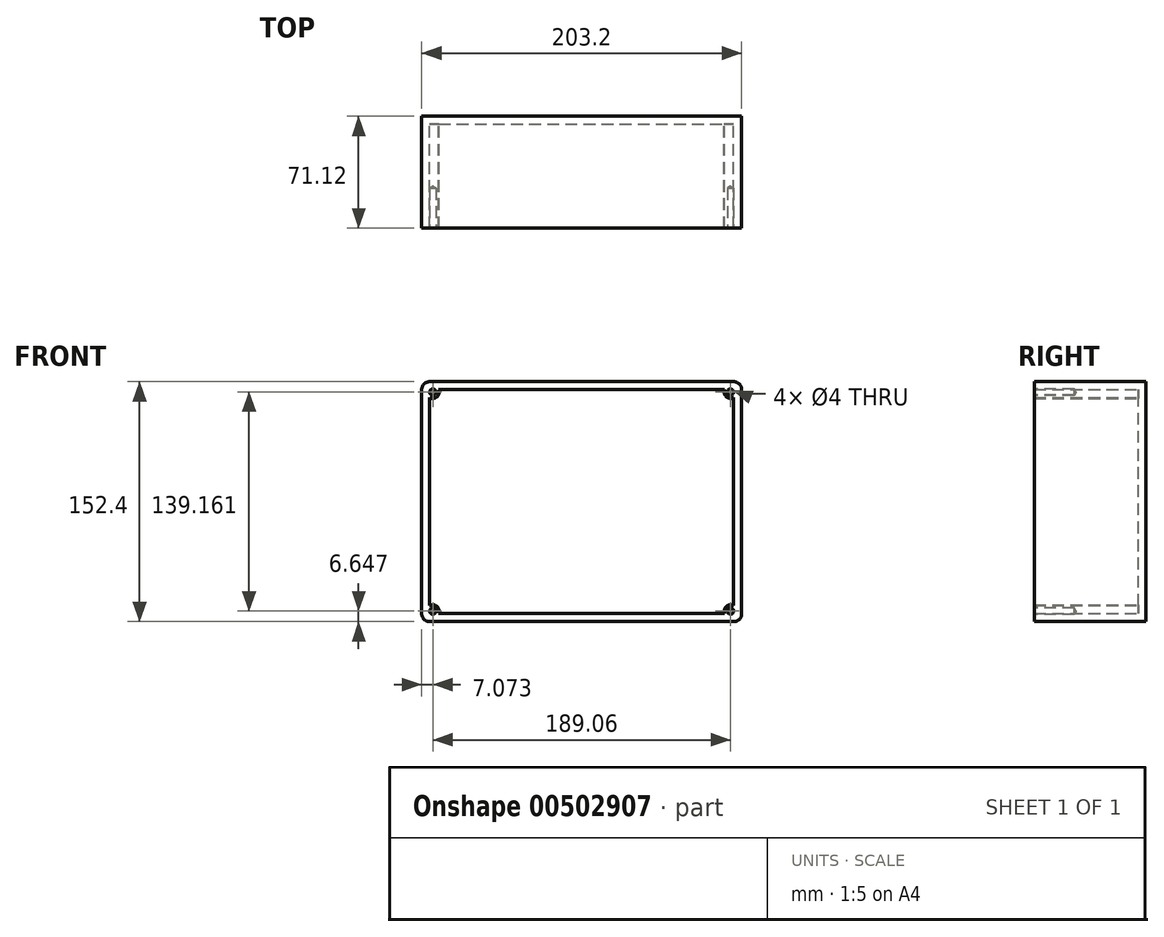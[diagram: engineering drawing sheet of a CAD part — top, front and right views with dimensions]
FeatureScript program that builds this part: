
annotation { "Feature Type Name" : "Feature", "Feature Type Description" : "" }
export const myFeature = defineFeature(function(context is Context, id is Id, definition is map)
    precondition{}
    {
        {
            var Q0;
            Q0=qCreatedBy(makeId("Front.planeOp"),FACE);
            var sketch = newSketch(context, id + "F0", { "sketchPlane" : qUnion([Q0])});
            skLineSegment(sketch, "E0.bottom", {"start": v(0, 0) * mm, "end": v(203.2, 0) * mm});
            skLineSegment(sketch, "E0.top", {"start": v(0, 152.4) * mm, "end": v(203.2, 152.4) * mm});
            skLineSegment(sketch, "E0.left", {"start": v(0, 0) * mm, "end": v(0, 152.4) * mm});
            skLineSegment(sketch, "E0.right", {"start": v(203.2, 0) * mm, "end": v(203.2, 152.4) * mm});
            skSolve(sketch);
        }
        {
            var Q0;
            Q0=makeQuery(id+"F0.imprint","IMPRINT",FACE,{"disambiguationData":[TD([[makeQuery(id+"F0.imprint","IMPRINT",EDGE,{"derivedFrom":sQuery(id+"F0.wireOp",EDGE,"E0.bottom")}),1.0]])]});
            extrude(context, id + "F1", {"entities" : qUnion([Q0]), "depth" : 71.12 * mm});
        }
        {
            var Q0;
            Q0=makeQuery(id+"F1.opExtrude","SWEPT_EDGE",EDGE,{"disambiguationData":[OSD([sQuery(id+"F0.wireOp",EDGE,"E0.top"),sQuery(id+"F0.wireOp",EDGE,"E0.left")])]});
            var Q1;
            Q1=makeQuery(id+"F1.opExtrude","SWEPT_EDGE",EDGE,{"disambiguationData":[OSD([sQuery(id+"F0.wireOp",EDGE,"E0.bottom"),sQuery(id+"F0.wireOp",EDGE,"E0.left")])]});
            var Q2;
            Q2=makeQuery(id+"F1.opExtrude","SWEPT_EDGE",EDGE,{"disambiguationData":[OSD([sQuery(id+"F0.wireOp",EDGE,"E0.top"),sQuery(id+"F0.wireOp",EDGE,"E0.right")])]});
            var Q3;
            Q3=makeQuery(id+"F1.opExtrude","SWEPT_EDGE",EDGE,{"disambiguationData":[OSD([sQuery(id+"F0.wireOp",EDGE,"E0.bottom"),sQuery(id+"F0.wireOp",EDGE,"E0.right")])]});
            fillet(context, id + "F2", {"entities" : qUnion([Q0, Q1, Q2, Q3]), "radius" : 5.08 * mm, "tangentPropagation" : true, "allowEdgeOverflow" : false});
        }
        {
            var Q0;
            Q0=makeQuery(id+"F1.opExtrude","CAP_FACE",FACE,{"disambiguationData":[OSD([sQuery(id+"F0.wireOp",EDGE,"E0.bottom"),sQuery(id+"F0.wireOp",EDGE,"E0.top"),sQuery(id+"F0.wireOp",EDGE,"E0.left"),sQuery(id+"F0.wireOp",EDGE,"E0.right")])],"isStart":false});
            shell(context, id + "F3", {"entities" : qUnion([Q0]), "thickness" : 5.08 * mm});
        }
        {
            var Q0;
            Q0=qCreatedBy(makeId("Front.planeOp"),FACE);
            var sketch = newSketch(context, id + "F4", { "sketchPlane" : qUnion([Q0])});
            skCircle(sketch, "E1", {"center": v(7.07, 145.75) * mm, "radius": 4 * mm});
            skCircle(sketch, "E2", {"center": v(196.08, 145.8) * mm, "radius": 4 * mm});
            skCircle(sketch, "E3", {"center": v(7.08, 6.65) * mm, "radius": 4 * mm});
            skCircle(sketch, "E4", {"center": v(196.13, 6.66) * mm, "radius": 4 * mm});
            skSolve(sketch);
        }
        {
            var Q0;
            Q0 = qSketchRegion(id + "F4", true);
            extrude(context, id + "F5", {"entities" : qUnion([Q0]), "operationType" : NewBodyOperationType.ADD, "depth" : 71.12 * mm});
        }
        {
            var Q0;
            Q0=makeQuery(id+"F5.boolean.opBoolean","MERGE",FACE,{"derivedFrom":[makeQuery(id+"F1.opExtrude","CAP_FACE",FACE,{"disambiguationData":[OSD([sQuery(id+"F0.wireOp",EDGE,"E0.bottom"),sQuery(id+"F0.wireOp",EDGE,"E0.top"),sQuery(id+"F0.wireOp",EDGE,"E0.left"),sQuery(id+"F0.wireOp",EDGE,"E0.right")])],"isStart":false}),makeQuery(id+"F5.opExtrude","CAP_FACE",FACE,{"disambiguationData":[OSD([sQuery(id+"F4.wireOp",EDGE,"E1")])],"isStart":false}),makeQuery(id+"F5.opExtrude","CAP_FACE",FACE,{"disambiguationData":[OSD([sQuery(id+"F4.wireOp",EDGE,"E2")])],"isStart":false}),makeQuery(id+"F5.opExtrude","CAP_FACE",FACE,{"disambiguationData":[OSD([sQuery(id+"F4.wireOp",EDGE,"E3")])],"isStart":false}),makeQuery(id+"F5.opExtrude","CAP_FACE",FACE,{"disambiguationData":[OSD([sQuery(id+"F4.wireOp",EDGE,"E4")])],"isStart":false})]});
            var sketch = newSketch(context, id + "F6", { "sketchPlane" : qUnion([Q0])});
            skCircle(sketch, "E5", {"center": v(7.07, 145.75) * mm, "radius": 4 * mm});
            skPoint(sketch, "E5.first.point", {"position": v(5.08, 142.28) * mm});
            skPoint(sketch, "E5.second.point", {"position": v(10.75, 147.32) * mm});
            skPoint(sketch, "E5.third.point", {"position": v(9.73, 142.76) * mm});
            skCircle(sketch, "E6", {"center": v(7.08, 6.65) * mm, "radius": 4 * mm});
            skPoint(sketch, "E6.first.point", {"position": v(5.08, 10.11) * mm});
            skPoint(sketch, "E6.second.point", {"position": v(10.76, 5.08) * mm});
            skPoint(sketch, "E6.third.point", {"position": v(9.73, 9.64) * mm});
            skCircle(sketch, "E7", {"center": v(196.13, 6.66) * mm, "radius": 4 * mm});
            skPoint(sketch, "E7.first.point", {"position": v(192.46, 5.08) * mm});
            skPoint(sketch, "E7.second.point", {"position": v(198.12, 10.13) * mm});
            skPoint(sketch, "E7.third.point", {"position": v(193.46, 9.64) * mm});
            skCircle(sketch, "E8", {"center": v(196.08, 145.8) * mm, "radius": 4 * mm});
            skPoint(sketch, "E8.first.point", {"position": v(192.37, 147.32) * mm});
            skPoint(sketch, "E8.second.point", {"position": v(198.12, 142.37) * mm});
            skPoint(sketch, "E8.third.point", {"position": v(194.04, 142.37) * mm});
            skSolve(sketch);
        }
        {
            var Q0;
            Q0=sQuery(id+"F6.wireOp",VERTEX,"E5.center");
            var Q1;
            Q1=sQuery(id+"F6.wireOp",VERTEX,"E6.center");
            var Q2;
            Q2=sQuery(id+"F6.wireOp",VERTEX,"E7.center");
            var Q3;
            Q3=sQuery(id+"F6.wireOp",VERTEX,"E8.center");
            var Q4;
            Q4=makeQuery(id+"F1.opExtrude","SWEPT_BODY",BODY,{"disambiguationData":[OSD([sQuery(id+"F0.wireOp",EDGE,"E0.bottom"),sQuery(id+"F0.wireOp",EDGE,"E0.top"),sQuery(id+"F0.wireOp",EDGE,"E0.left"),sQuery(id+"F0.wireOp",EDGE,"E0.right")])]});
            hole(context, id + "F7", {"style" : HoleStyle.SIMPLE, "endStyle" : HoleEndStyle.BLIND, "holeDiameter" : 4 * mm, "holeDepth" : 25.4 * mm, "isTappedThrough" : true, "tappedDepth" : 12.7 * mm, "tapClearance" : 3, "startFromSketch" : true, "locations" : qUnion([Q0, Q1, Q2, Q3]), "scope" : qUnion([Q4])});
        }
    });
